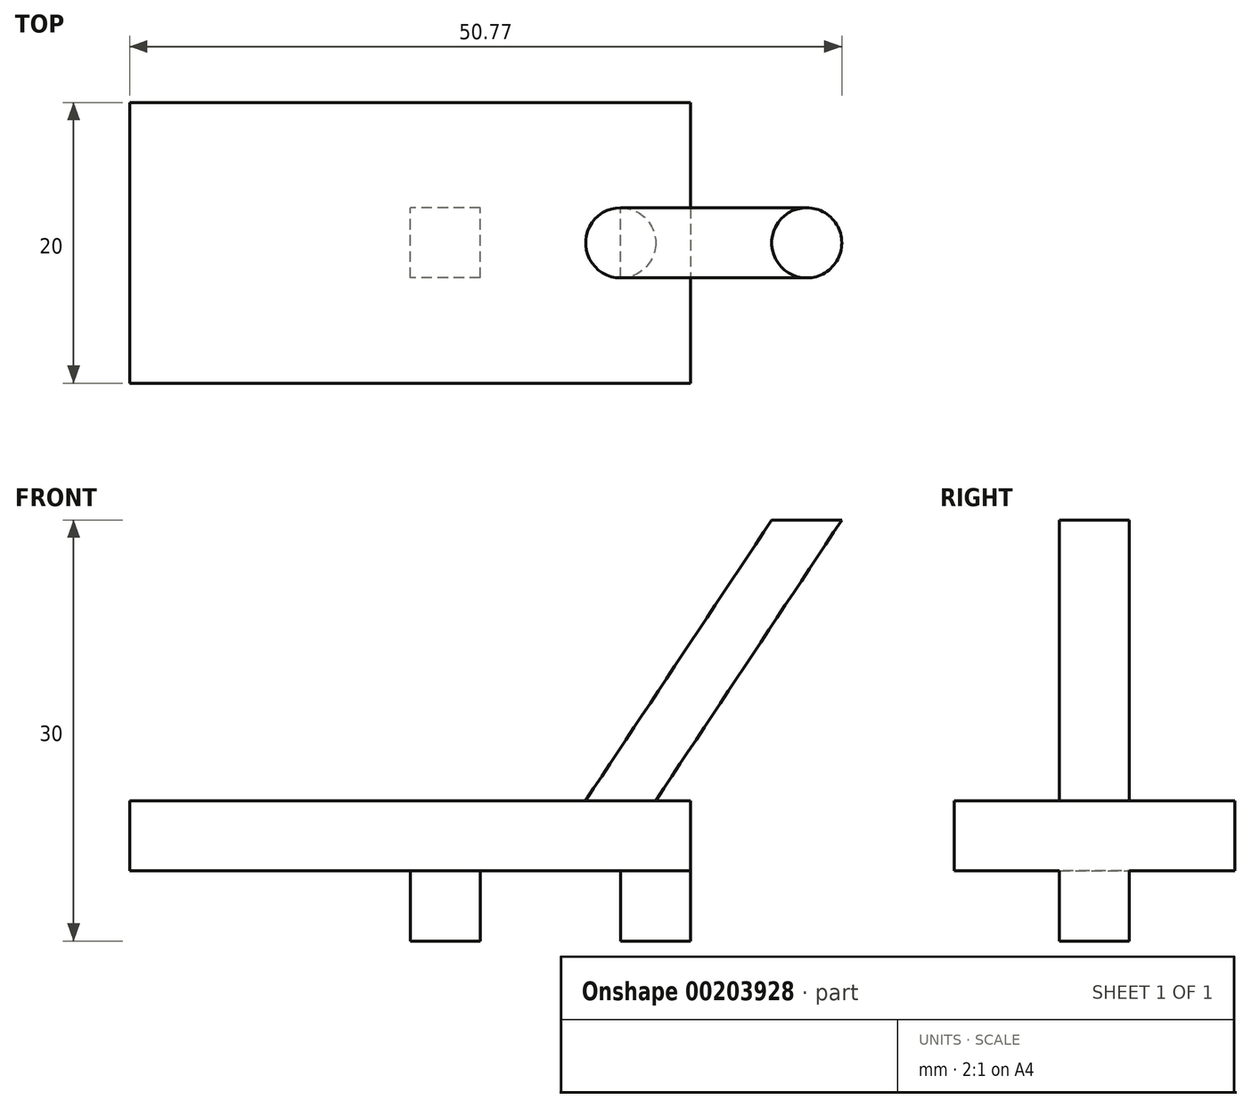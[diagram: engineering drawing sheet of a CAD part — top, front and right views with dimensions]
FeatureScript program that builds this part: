
annotation { "Feature Type Name" : "Feature", "Feature Type Description" : "" }
export const myFeature = defineFeature(function(context is Context, id is Id, definition is map)
    precondition{}
    {
        {
            var Q0;
            Q0=qCreatedBy(makeId("Top.planeOp"),FACE);
            var sketch = newSketch(context, id + "F0", { "sketchPlane" : qUnion([Q0])});
            skLineSegment(sketch, "E0.bottom", {"start": v(20, 10) * mm, "end": v(-20, 10) * mm});
            skLineSegment(sketch, "E0.top", {"start": v(20, -10) * mm, "end": v(-20, -10) * mm});
            skLineSegment(sketch, "E0.left", {"start": v(20, 10) * mm, "end": v(20, -10) * mm});
            skLineSegment(sketch, "E0.right", {"start": v(-20, 10) * mm, "end": v(-20, -10) * mm});
            skPoint(sketch, "E0.middle", {"position": v(0, 0) * mm});
            skSolve(sketch);
        }
        {
            var Q0;
            Q0=qSketchRegion(id+"F0",true);
            extrude(context, id + "F1", {"entities" : qUnion([Q0]), "depth" : 5 * mm});
        }
        {
            var Q0;
            Q0=makeQuery(id+"F1.opExtrude","CAP_FACE",FACE,{"disambiguationData":[OSD([sQuery(id+"F0.wireOp",EDGE,"E0.bottom"),sQuery(id+"F0.wireOp",EDGE,"E0.top"),sQuery(id+"F0.wireOp",EDGE,"E0.left"),sQuery(id+"F0.wireOp",EDGE,"E0.right")])],"isStart":true});
            var sketch = newSketch(context, id + "F2", { "sketchPlane" : qUnion([Q0])});
            skLineSegment(sketch, "E1", {"start": v(20, 2.5) * mm, "end": v(15, 2.5) * mm});
            skLineSegment(sketch, "E2", {"start": v(15, 2.5) * mm, "end": v(15, -2.5) * mm});
            skLineSegment(sketch, "E3", {"start": v(15, -2.5) * mm, "end": v(20, -2.5) * mm});
            skLineSegment(sketch, "E4", {"start": v(20, -2.5) * mm, "end": v(20, 0) * mm});
            skLineSegment(sketch, "E5", {"start": v(20, 0) * mm, "end": v(20, 2.5) * mm});
            skLineSegment(sketch, "E6.bottom", {"start": v(5, 2.5) * mm, "end": v(0, 2.5) * mm});
            skLineSegment(sketch, "E6.top", {"start": v(5, -2.5) * mm, "end": v(0, -2.5) * mm});
            skLineSegment(sketch, "E6.left", {"start": v(5, 2.5) * mm, "end": v(5, -2.5) * mm});
            skLineSegment(sketch, "E6.right", {"start": v(0, 2.5) * mm, "end": v(0, -2.5) * mm});
            skPoint(sketch, "E6.middle", {"position": v(2.5, 0) * mm});
            skSolve(sketch);
        }
        {
            var Q0;
            Q0=qSketchRegion(id+"F2",true);
            extrude(context, id + "F3", {"entities" : qUnion([Q0]), "operationType" : NewBodyOperationType.ADD, "depth" : 5 * mm});
        }
        {
            var Q0;
            Q0=makeQuery(id+"F1.opExtrude","CAP_FACE",FACE,{"disambiguationData":[OSD([sQuery(id+"F0.wireOp",EDGE,"E0.bottom"),sQuery(id+"F0.wireOp",EDGE,"E0.top"),sQuery(id+"F0.wireOp",EDGE,"E0.left"),sQuery(id+"F0.wireOp",EDGE,"E0.right")])],"isStart":false});
            var sketch = newSketch(context, id + "F4", { "sketchPlane" : qUnion([Q0])});
            skCircle(sketch, "E7", {"center": v(15, 0) * mm, "radius": 2.5 * mm});
            skSolve(sketch);
        }
        {
            var Q0;
            Q0=makeQuery(id+"F1.opExtrude","SWEPT_FACE",FACE,{"disambiguationData":[OSD([sQuery(id+"F0.wireOp",EDGE,"E0.top")])]});
            var sketch = newSketch(context, id + "F5", { "sketchPlane" : qUnion([Q0])});
            skLineSegment(sketch, "E8", {"start": v(0, 0) * mm, "end": v(16.58, 25) * mm});
            skSolve(sketch);
        }
        {
            var Q0;
            Q0=makeQuery(id+"F4.imprint","IMPRINT",FACE,{"disambiguationData":[TD([[makeQuery(id+"F4.imprint","IMPRINT",EDGE,{"derivedFrom":sQuery(id+"F4.wireOp",EDGE,"E7")}),1.0]])]});
            var Q1;
            Q1=sQuery(id+"F5.wireOp",EDGE,"E8");
            sweep(context, id + "F6", {"operationType" : NewBodyOperationType.ADD, "profiles" : qUnion([Q0]), "path" : qUnion([Q1])});
        }
    });
